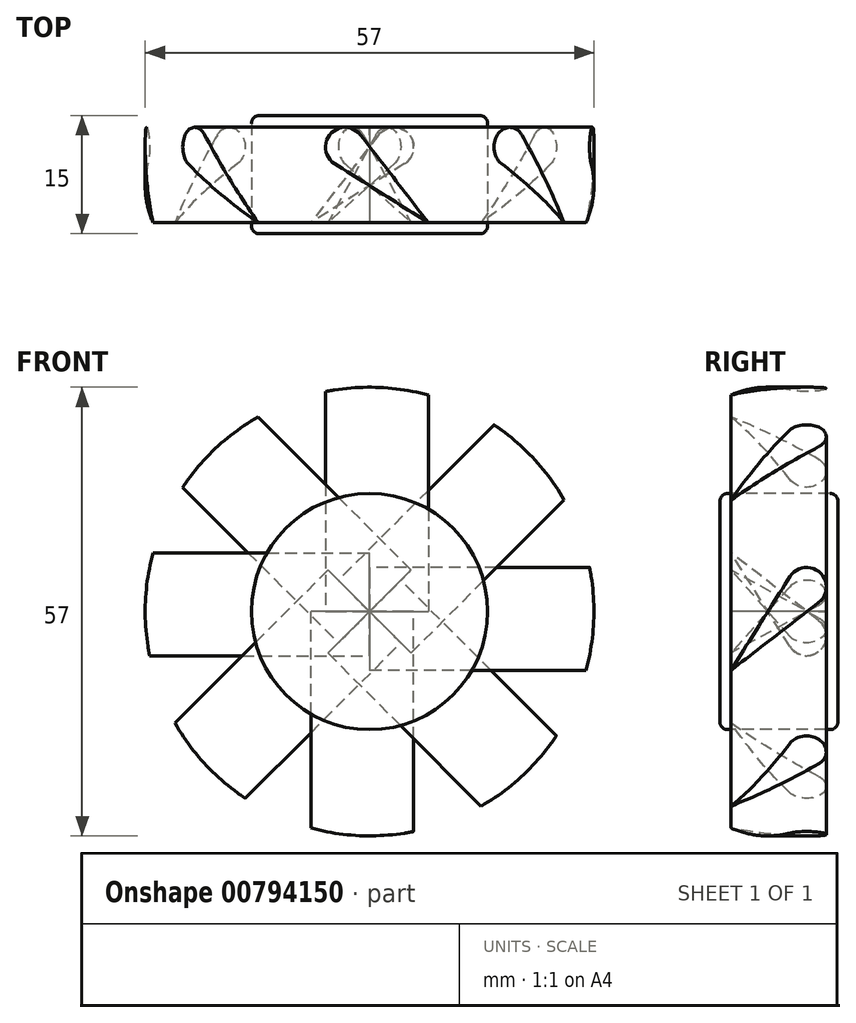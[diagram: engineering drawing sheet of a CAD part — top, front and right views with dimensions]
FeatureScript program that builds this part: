
annotation { "Feature Type Name" : "Feature", "Feature Type Description" : "" }
export const myFeature = defineFeature(function(context is Context, id is Id, definition is map)
    precondition{}
    {
        {
            var Q0;
            Q0=qCreatedBy(makeId("Front.planeOp"),FACE);
            var sketch = newSketch(context, id + "F0", { "sketchPlane" : qUnion([Q0])});
            skCircle(sketch, "E0", {"center": v(0, 0) * mm, "radius": 29 * mm});
            skLineSegment(sketch, "E1.bottom", {"start": v(30, -30) * mm, "end": v(-30, -30) * mm});
            skLineSegment(sketch, "E1.top", {"start": v(30, 30) * mm, "end": v(-30, 30) * mm});
            skLineSegment(sketch, "E1.left", {"start": v(30, -30) * mm, "end": v(30, 30) * mm});
            skLineSegment(sketch, "E1.right", {"start": v(-30, -30) * mm, "end": v(-30, 30) * mm});
            skLineSegment(sketch, "E2.bottom", {"start": v(25, -25) * mm, "end": v(-25, -25) * mm, "construction": true});
            skLineSegment(sketch, "E2.top", {"start": v(25, 25) * mm, "end": v(-25, 25) * mm, "construction": true});
            skLineSegment(sketch, "E2.left", {"start": v(25, -25) * mm, "end": v(25, 25) * mm, "construction": true});
            skLineSegment(sketch, "E2.right", {"start": v(-25, -25) * mm, "end": v(-25, 25) * mm, "construction": true});
            skCircle(sketch, "E3", {"center": v(-25, 25) * mm, "radius": 1.5 * mm});
            skCircle(sketch, "E4", {"center": v(25, 25) * mm, "radius": 1.5 * mm});
            skCircle(sketch, "E5", {"center": v(25, -25) * mm, "radius": 1.5 * mm});
            skCircle(sketch, "E6", {"center": v(-25, -25) * mm, "radius": 1.5 * mm});
            skSolve(sketch);
        }
        {
            var Q0;
            Q0=makeQuery(id+"F0.imprint","IMPRINT",FACE,{"disambiguationData":[TD([[makeQuery(id+"F0.imprint","IMPRINT",EDGE,{"derivedFrom":sQuery(id+"F0.wireOp",EDGE,"E0")}),-1.0]])]});
            extrude(context, id + "F1", {"entities" : qUnion([Q0]), "oppositeDirection" : true, "depth" : 15 * mm, "offsetDistance" : 25 * mm});
        }
        {
            var Q0;
            Q0=qCreatedBy(makeId("Right.planeOp"),FACE);
            var sketch = newSketch(context, id + "F2", { "sketchPlane" : qUnion([Q0])});
            skLineSegment(sketch, "E7", {"start": v(0, 0) * mm, "end": v(-17.7, 0) * mm, "construction": true});
            skPoint(sketch, "E8.0", {"position": v(0, 0) * mm});
            skCircle(sketch, "E9", {"center": v(11.01, 3.11) * mm, "radius": 2.5 * mm, "construction": true});
            skLineSegment(sketch, "E10", {"start": v(11.01, 3.11) * mm, "end": v(1.41, -7.46) * mm});
            skLineSegment(sketch, "E11", {"start": v(8.9, 4.45) * mm, "end": v(1.41, -7.46) * mm});
            skLineSegment(sketch, "E12", {"start": v(12.54, 1.14) * mm, "end": v(1.41, -7.46) * mm});
            skArc(sketch, "E13", {"start": v(8.9, 4.45) * mm, "mid": v(12.7, 4.97) * mm, "end": v(12.54, 1.14) * mm});
            skLineSegment(sketch, "E14.0", {"start": v(15, -30) * mm, "end": v(15, 30) * mm, "construction": true});
            skLineSegment(sketch, "E15", {"start": v(0, -9.28) * mm, "end": v(0, 9) * mm});
            skSolve(sketch);
        }
        {
            var Q0;
            Q0 = qSketchRegion(id + "F2", true);
            extrude(context, id + "F3", {"entities" : qUnion([Q0]), "depth" : 30 * mm, "offsetDistance" : 25 * mm});
        }
        {
            var Q0;
            Q0=makeQuery(id+"F3.opExtrude","SWEPT_BODY",BODY,{"disambiguationData":[OSD([sQuery(id+"F2.wireOp",EDGE,"E11"),sQuery(id+"F2.wireOp",EDGE,"E12"),sQuery(id+"F2.wireOp",EDGE,"E13")])]});
            var Q1;
            Q1=sQuery(id+"F2.wireOp",EDGE,"E7");
            circularPattern(context, id + "F4", {"entities" : qUnion([Q0]), "axis" : qUnion([Q1]), "angle" : 360 * degree, "instanceCount" : 8, "equalSpace" : true});
        }
        {
            var Q0;
            Q0=qCreatedBy(makeId("Front.planeOp"),FACE);
            var sketch = newSketch(context, id + "F5", { "sketchPlane" : qUnion([Q0])});
            skCircle(sketch, "E16", {"center": v(0, 0) * mm, "radius": 15 * mm});
            skSolve(sketch);
        }
        {
            var Q0;
            Q0 = qSketchRegion(id + "F5", true);
            extrude(context, id + "F6", {"entities" : qUnion([Q0]), "oppositeDirection" : true, "depth" : 15 * mm, "offsetDistance" : 25 * mm});
        }
        {
            var Q0;
            Q0=qCreatedBy(makeId("Front.planeOp"),FACE);
            var sketch = newSketch(context, id + "F7", { "sketchPlane" : qUnion([Q0])});
            skPoint(sketch, "E17.0", {"position": v(0, 0) * mm});
            skCircle(sketch, "E18", {"center": v(0, 0) * mm, "radius": 28.5 * mm});
            skCircle(sketch, "E19", {"center": v(0, 0) * mm, "radius": 50 * mm});
            skSolve(sketch);
        }
        {
            var Q0;
            Q0 = qSketchRegion(id + "F7", true);
            extrude(context, id + "F8", {"entities" : qUnion([Q0]), "operationType" : NewBodyOperationType.REMOVE, "endBound" : BoundingType.THROUGH_ALL, "oppositeDirection" : true, "depth" : 25 * mm, "offsetDistance" : 25 * mm});
        }
        {
            var Q0;
            Q0=makeQuery(id+"F6.opExtrude","CAP_EDGE",EDGE,{"disambiguationData":[OSD([sQuery(id+"F5.wireOp",EDGE,"E16")])],"isStart":true});
            var Q1;
            Q1=makeQuery(id+"F6.opExtrude","CAP_EDGE",EDGE,{"disambiguationData":[OSD([sQuery(id+"F5.wireOp",EDGE,"E16")])],"isStart":false});
            fillet(context, id + "F9", {"entities" : qUnion([Q0, Q1]), "radius" : 1 * mm, "tangentPropagation" : true, "allowEdgeOverflow" : false});
        }
    });
